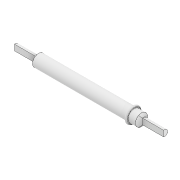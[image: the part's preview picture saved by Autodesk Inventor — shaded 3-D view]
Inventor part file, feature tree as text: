
AUTODESK INVENTOR PART (.ipt)
format: ipt  version: 2022 (Build 260153000, 153)  size: 181,760 bytes
history: native  units: mm
features: extrude x4, sketch x4, plane x3, thicken_offset x2, projected_geometry x2, other x2, loft x1, fillet x1, mirror x1
ambient origin geometry x8: Origin, YZ Plane, XZ Plane, XY Plane, X Axis, Y Axis, Z Axis, Center Point
bodies: Solid1 (feature_tree)
feature tree (20):
  extrude  "Shaft"  Depth=10.0mm TaperAngle=0.0deg
  plane  "Work Plane1"
  extrude  "Wheel Insert Profile"  Depth=7.5mm
  thicken_offset  "Thicken5"
  loft  "Loft1"
  plane  "Work Plane2"
  extrude  "Stopper"  Depth=2.0mm
  fillet  "Fillet1"  [1 undecoded]
  mirror  "Mirror1"
  plane  "Work Plane5"
  extrude  "Extrusion7"  Depth=0.05mm
  thicken_offset  "Thicken6"
  sketch  "Sketch1"  dims[d2=0.0mm d25=10.0mm d26=0.0mm]
  sketch  "Sketch3"  dims[d29=1.0mm d32=0.0mm d33=90.0deg d35=7.5mm]
  sketch  "Sketch4"  dims[d36=1.0mm d37=0.0mm d38=0.5mm]
  projected_geometry  "Projected Loop1"
  other  "Edges2"
  other  "Edges6"
  sketch  "Sketch10"  dims[d89=3.0mm d90=2.0mm d91=0.0mm d92=90.0deg d93=0.05mm d94=0.15mm d95=0.5mm d96=0.5mm d97=0.0mm d98=0.0mm d99=0.1mm d100=0.1mm d101=-14.5mm d102=-16.5mm d103=0.5mm d104=0.5mm]
  projected_geometry  "Project Cut Edges3"
note: 1 required parameter value undecoded (feature->parameter linkage not recoverable at this tier; creation-order binding heuristic only, values carry confidence <= 0.55)
